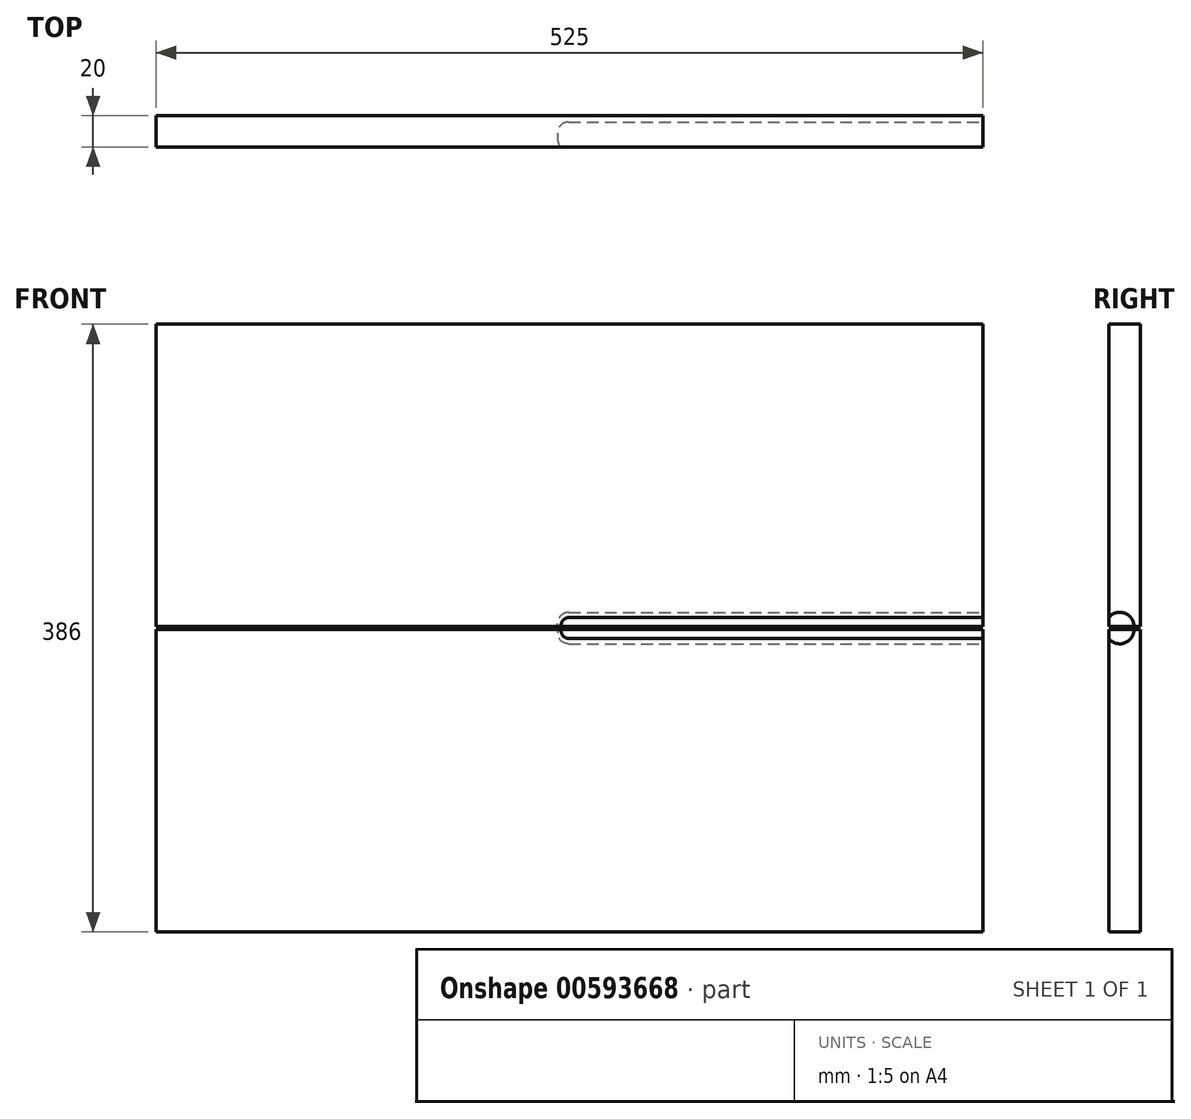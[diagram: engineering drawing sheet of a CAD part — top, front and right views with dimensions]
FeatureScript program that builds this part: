
annotation { "Feature Type Name" : "Feature", "Feature Type Description" : "" }
export const myFeature = defineFeature(function(context is Context, id is Id, definition is map)
    precondition{}
    {
        {
            var Q0;
            Q0=qCreatedBy(makeId("Front.planeOp"),FACE);
            var sketch = newSketch(context, id + "F0", { "sketchPlane" : qUnion([Q0])});
            skLineSegment(sketch, "E0.bottom", {"start": v(-261.44, 118.72) * mm, "end": v(263.56, 118.72) * mm});
            skLineSegment(sketch, "E0.top", {"start": v(-261.44, -73.28) * mm, "end": v(263.56, -73.28) * mm});
            skLineSegment(sketch, "E0.left", {"start": v(-261.44, 118.72) * mm, "end": v(-261.44, -73.28) * mm});
            skLineSegment(sketch, "E0.right", {"start": v(263.56, 118.72) * mm, "end": v(263.56, -73.28) * mm});
            skSolve(sketch);
        }
        {
            var Q0;
            Q0=makeQuery(id+"F0.imprint","IMPRINT",FACE,{"disambiguationData":[TD([[makeQuery(id+"F0.imprint","IMPRINT",EDGE,{"derivedFrom":sQuery(id+"F0.wireOp",EDGE,"E0.bottom")}),-1.0]])]});
            extrude(context, id + "F1", {"entities" : qUnion([Q0]), "oppositeDirection" : true, "depth" : 20 * mm, "offsetDistance" : 25 * mm});
        }
        {
            var Q0;
            Q0=makeQuery(id+"F1.opExtrude","SWEPT_FACE",FACE,{"disambiguationData":[OSD([sQuery(id+"F0.wireOp",EDGE,"E0.right")])]});
            var sketch = newSketch(context, id + "F2", { "sketchPlane" : qUnion([Q0])});
            skCircle(sketch, "E1", {"center": v(7, -73.28) * mm, "radius": 9 * mm});
            skSolve(sketch);
        }
        {
            var Q0;
            {var subQ0=sQuery(id+"F2.wireOp",EDGE,"E1");var subQ1=sQuery(id+"F0.wireOp",EDGE,"E0.right");var subQ4=makeQuery(id+"F1.opExtrude","CAP_EDGE",EDGE,{"disambiguationData":[OSD([subQ1])],"isStart":true});var subQ5=makeQuery(id+"F2.imprint","INTERSECT",VERTEX,{"derivedFrom":[subQ4,subQ0]});Q0=makeQuery(id+"F2.imprint","IMPRINT",FACE,{"disambiguationData":[TD([[makeQuery(id+"F2.imprint","IMPRINT",EDGE,{"disambiguationData":[TD([[subQ5,-1.0]])],"derivedFrom":subQ0}),1.0]])]});}
            var Q1;
            {var subQ0=sQuery(id+"F2.wireOp",EDGE,"E1");var subQ1=sQuery(id+"F0.wireOp",EDGE,"E0.right");var subQ4=makeQuery(id+"F1.opExtrude","CAP_EDGE",EDGE,{"disambiguationData":[OSD([subQ1])],"isStart":true});var subQ5=makeQuery(id+"F2.imprint","INTERSECT",VERTEX,{"derivedFrom":[subQ4,subQ0]});Q1=makeQuery(id+"F2.imprint","IMPRINT",FACE,{"disambiguationData":[TD([[makeQuery(id+"F2.imprint","IMPRINT",EDGE,{"disambiguationData":[TD([[subQ5,1.0]])],"derivedFrom":subQ0}),1.0]])]});}
            extrude(context, id + "F3", {"entities" : qUnion([Q0, Q1]), "operationType" : NewBodyOperationType.REMOVE, "oppositeDirection" : true, "depth" : 270 * mm, "offsetDistance" : 25 * mm});
        }
        {
            var Q0;
            Q0=makeQuery(id+"F3.boolean.opBoolean","COPY",EDGE,{"derivedFrom":makeQuery(id+"F3.opExtrude","CAP_EDGE",EDGE,{"disambiguationData":[OSD([sQuery(id+"F2.wireOp",EDGE,"E1")])],"isStart":false})});
            fillet(context, id + "F4", {"entities" : qUnion([Q0]), "radius" : 7 * mm, "tangentPropagation" : true, "allowEdgeOverflow" : false});
        }
        {
            var Q0;
            Q0=makeQuery(id+"F1.opExtrude","CAP_FACE",FACE,{"disambiguationData":[OSD([sQuery(id+"F0.wireOp",EDGE,"E0.bottom"),sQuery(id+"F0.wireOp",EDGE,"E0.top"),sQuery(id+"F0.wireOp",EDGE,"E0.left"),sQuery(id+"F0.wireOp",EDGE,"E0.right")])],"isStart":true});
            var sketch = newSketch(context, id + "F5", { "sketchPlane" : qUnion([Q0])});
            skLineSegment(sketch, "E2", {"start": v(-94.07, -74.28) * mm, "end": v(-12.9, -74.28) * mm});
            skSolve(sketch);
        }
        {
            var Q0;
            Q0=sQuery(id+"F5.wireOp",EDGE,"E2");
            extrude(context, id + "F6", {"bodyType" : ToolBodyType.SURFACE, "surfaceEntities" : qUnion([Q0]), "oppositeDirection" : true, "depth" : 50 * mm, "offsetDistance" : 25 * mm});
        }
        {
            var Q0;
            Q0=makeQuery(id+"F1.opExtrude","SWEPT_BODY",BODY,{"disambiguationData":[OSD([sQuery(id+"F0.wireOp",EDGE,"E0.bottom"),sQuery(id+"F0.wireOp",EDGE,"E0.top"),sQuery(id+"F0.wireOp",EDGE,"E0.left"),sQuery(id+"F0.wireOp",EDGE,"E0.right")])]});
            var Q1;
            Q1=makeQuery(id+"F6.opExtrude","SWEPT_FACE",FACE,{"disambiguationData":[OSD([sQuery(id+"F5.wireOp",EDGE,"E2")])]});
            mirror(context, id + "F7", {"entities" : qUnion([Q0]), "mirrorPlane" : qUnion([Q1])});
        }
    });
